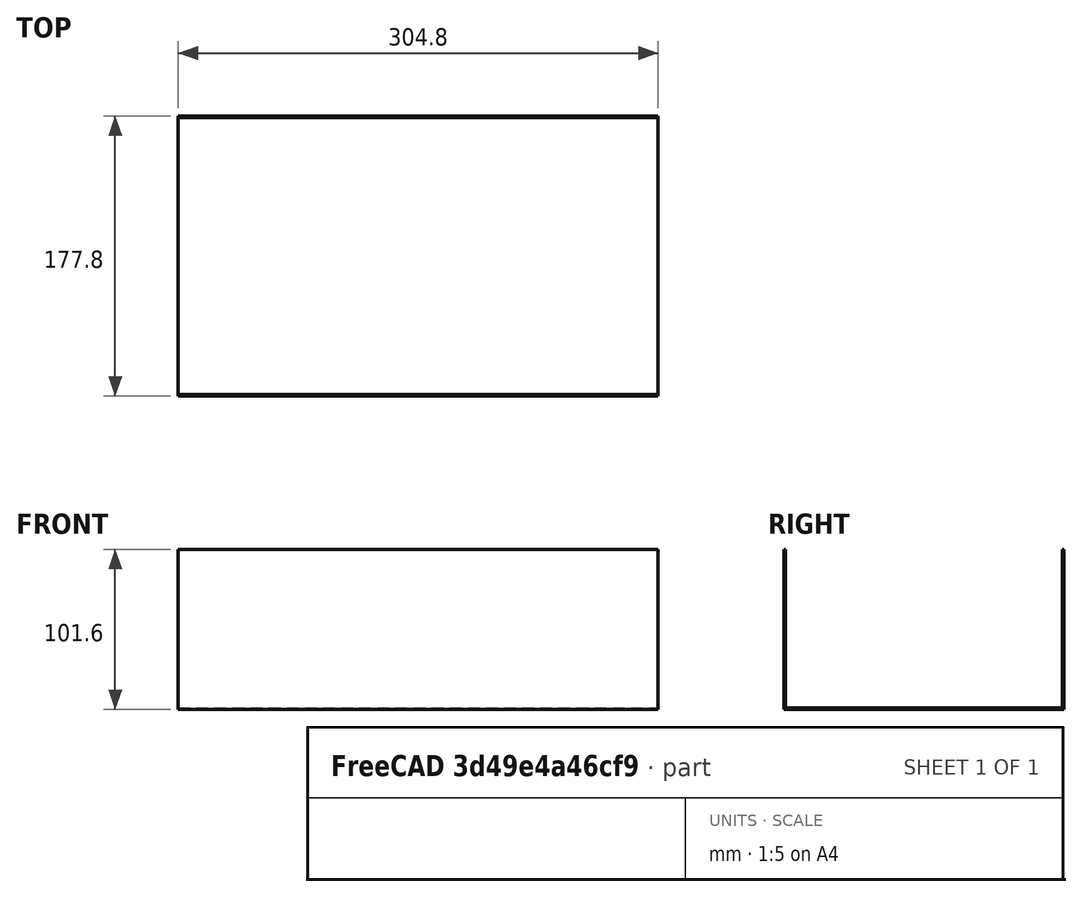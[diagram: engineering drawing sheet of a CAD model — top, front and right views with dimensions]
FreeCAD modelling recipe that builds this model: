
FCSTD DOCUMENT  (FreeCAD 0.17R10993 (Git))
Label: bud_12_7_4
License: All rights reserved
LicenseURL: http://en.wikipedia.org/wiki/All_rights_reserved
objects: Sketcher::SketchObject×1, PartDesign::Pad×1, PartDesign::Body×1
note: 4 computed .brp shape members not serialized (recipe doc carries the construction recipe); baked Part::Feature solids carry a one-line shape summary decoded from their .brp

FEATURE [Sketcher::SketchObject] Sketch
  MapMode = 5
  Placement = pos=(0,0,0) rot=(0.57735,0.57735,0.57735;2.0944rad)
  Support = -> [YZ_Plane]
  sketch-geometry (9):
    g0: LineSegment StartX=-88.9 StartY=100.584 StartZ=0 EndX=-88.9 EndY=-1.016 EndZ=0
    g1: LineSegment StartX=-88.9 StartY=-1.016 StartZ=0 EndX=88.9 EndY=-1.016 EndZ=0
    g2: LineSegment StartX=88.9 StartY=-1.016 StartZ=0 EndX=88.9 EndY=100.584 EndZ=0
    g3: LineSegment StartX=88.9 StartY=100.584 StartZ=0 EndX=87.884 EndY=100.584 EndZ=0
    g4: LineSegment StartX=87.884 StartY=100.584 StartZ=0 EndX=87.884 EndY=0 EndZ=0
    g5: LineSegment StartX=-87.884 StartY=0 StartZ=0 EndX=-87.884 EndY=100.584 EndZ=0
    g6: LineSegment StartX=-87.884 StartY=100.584 StartZ=0 EndX=-88.9 EndY=100.584 EndZ=0
    g7: LineSegment StartX=87.884 StartY=0 StartZ=0 EndX=-87.884 EndY=0 EndZ=0
    g8: LineSegment [constr] StartX=-87.884 StartY=0 StartZ=0 EndX=-87.884 EndY=-1.016 EndZ=0
  constraints (26):
    c: Vertical(g0)
    c: Coincident(g0,g1)
    c: Horizontal(g1)
    c: Coincident(g1,g2)
    c: Vertical(g2)
    c: Coincident(g2,g3)
    c: Coincident(g3,g4)
    c: Vertical(g4)
    c: Vertical(g5)
    c: Coincident(g5,g6)
    c: Coincident(g6,g0)
    c: DistanceX(g1,g1) = 177.8
    c: DistanceX(g6,g6) = 1.016
    c: Horizontal(g6)
    c: Horizontal(g3)
    c: DistanceY(g0,g0) = 101.6
    c: Equal(g2,g0)
    c: Coincident(g7,g4)
    c: Coincident(g7,g5)
    c: Horizontal(g7)
    c: Equal(g3,g6)
    c: Symmetric(g7,g7,g-1)
    c: Coincident(g8,g5)
    c: PointOnObject(g8,g1)
    c: Vertical(g8)
    c: Equal(g8,g6)
FEATURE [PartDesign::Pad] Pad
  Length = 304.8
  Length2 = 100
  Midplane = true
  Placement = pos=(0,0,0) rot=(0.57735,0.57735,0.57735;2.0944rad)
  Profile = -> Sketch
  Type = 0
FEATURE [PartDesign::Body] Body
  Group = -> [Sketch,Pad]
  Origin = -> BodyOrigin
  Tip = -> Pad
